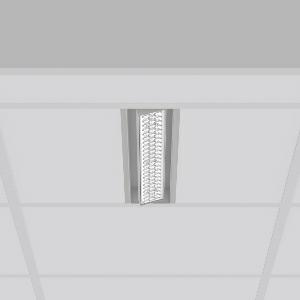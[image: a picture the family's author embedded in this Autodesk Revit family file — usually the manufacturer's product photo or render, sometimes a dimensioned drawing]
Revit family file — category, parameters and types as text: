
# Revit family: tx-move_901729_004_11a8
name_source: partatom
category: Lighting Fixtures
units: mm (PartAtom-declared; Revit-internal decimal feet)

## family parameters
Cut with Voids When Loaded = No
Host = Face
Light Source = No
Part Type = Normal
Room Calculation Point = No
Round Connector Dimension = Use Diameter
Shared = No

## types (1)
- MultiLumen 1 (1 x LED Modul 830, 2850 lm, 3000)
    Apparent Load = 18 VA
    Approval mark = CE
    CIE Flux Codes = 77 96 99 100 100
    Color Rendering = 80
    Color Temperature = 3000
    Default Elevation = 1800 mm
    Description = Series: TX-MOVE
Einlege/Einbau-Flächenstrahler. Housing: sheet steel, powder-coated. Swivel range: 90°. High-efficiency LED units with optimum light control thanks to clear plastic (PC) lens optics. Spezielle Mikrostrukturen reduzieren Gelbsaum. Symmetrical light distribution. Suitable for laying in grid ceiling module 625. Connected converter included in separate gearbox.Suitable for through-wiring.MultiLumen: Luminous flux adjustable in 3 steps. Accessories: Mounting frame for installation in suspended ceilings. Environmentally friendly and resource-saving due to replaceable and recyclable components. 
Colour: silver, matt (approx. RAL 9006)
Length: 622 mm
Width: 116 mm
Height: 39 mm
Cut-out length: 602 mm
Cut-out width: 98 mm
Recess height: 100 mm
Lamp: LED
Socket: without socket
Colour temperature: 3000K
Colour rendering index (CRI): 80
System power: 18 W
Rated luminous flux: 2850 lm
Luminous efficiency: 158 lm/W
System power 2: 26 W
Rated luminous flux 2: 3950 lm
Luminous efficiency 2: 152 lm/W
System power 3: 39 W
Rated luminous flux 3: 5550 lm
Luminous efficiency 3: 142 lm/W
Control gear: Regulated power supply
Protection class: I
Type of protection: IP 20
    Height = 0 mm  [stored 0 ft]
    Lamp = 1 x LED Modul 830
    Lamp Light Flux = 2850 lm
    Lamp count = 1
    Length = 622 mm
    Lifetime = 50000 h
    Luminous efficacy = 158 lm/W
    Manufacturer = RZB
    ModVariant = No
    Model = 901729.004
    Mounting Place = Ceiling, Wall
    Mounting Type = Recessed
    Number of Poles = 1
    OnlyDefault = Yes
    Power Factor = 1
    Product Name = TX-MOVE
    Product group = Recessed projectors
    ProductGroupID = 401
    Protection Class = Protection class I
    Protection Degree = IP 20
    RLX_Detail_Level = 1
    RLX_Emergency_Light_Flux = 0 lm
    RLX_Emergency_Type = 0
    RLX_Emergency_Type_DB = No
    RlxData = <blob elided: 27325 chars, md5=1cb3a9a1>
    Socket = socket
    Standby Power = 0 W
    System Light Flux = 2850 lm
    System Power = 18 W
    Type Comments = MultiLumen 1
    Type Image = 901729.004.jpg
    URL = http://relux.com
    VarID = multilumen_1
    Voltage = 230 V
    Voltage Range = 220-240 V
    Weight = 0.00 kg
    Width = 116 mm

note: [stored X ft] marks values corroborated as IEEE doubles in the binary element streams (Revit-internal decimal feet)

## geometry (parser evidence)
native form markers: Blend x4, Sweep x11
no freeform markers — native parametric forms only
